# Revit family: QF_BPRO_RWRR 161_572938
name_source: partatom
category: Sonderausstattung
revit_build: Autodesk Revit 2018 (Build: 20190510_1515(x64)
units: mm (PartAtom-declared; Revit-internal decimal feet)

## family parameters
Arbeitsebenenbasiert = Nein
Beim Laden mit Abzugskörper schneiden = Nein
Bemaßung runder Anschluss = Durchmesser verwenden
Gemeinsam genutzt = Nein
Immer vertikal = Ja
Raumberechnungspunkt = Ja
Teiletyp = Normal

## types (1)
- RWRR 161
    Abstand Einlagen = 73 mm
    Anzahl Schienen = 18
    Artikel Nummer = 572938
    Beschreibung = Regalwagen aus rostfreiem Edelstahl
im leeren Zustand raumsparend ineinander zu schieben
Auflagenabstand: 18 Paar 73 mm
Kapazität: 18 GN 2/1 oder  36 GN 1/1
Tragfähigkeit: 200 kg
Wandabweiser aus Kunststoff (Polyamid) an allen vier Ecken
    Beschreibung durch Hersteller analog Leistungsverzeichniskurztext = Abmessungen

Länge:			 662 mm
Breite:			  734 mm
Höhe:			1645 mm

Lichtes Maß:
Abstand der Auflagenschienen:	    73 mm


Ausführung

Der Regalwagen besteht aus CNS 18/10, Werkstoff-Nr. 1.4301. Zwischen stabilem Vierkant-rohr mit 25 x 25 mm (gebogen ohne Einzug) befinden sich eingeschweißte U-Profil-Führungsschienen. Diese sind mit einer Kippsicherung sowie einer beidseitigen Durchschubsicherung für GN 2/1, 1/1 und 2/4 versehen.

Durch diagonal angeordnete Querverstrebungen
50 x 25 mm lassen sich die RWRR 161 im leeren Zustand raumsparend ineinander schieben.
Für zusätzliche Stabilität sorgen 2 einhängbare CNS-Bügel aus Rundmaterial, die auf der Vorder- und Rückseite auf halber Höhe angebracht sind und nach der Bestückung in die dafür vorgesehenen Ösen eingehängt werden.

Der Regalwagen ist fahrbar mittels rostfreien Kunststoffrollen gemäß DIN 18867, Teil 8
(4 Lenkrollen, davon 2 mit Feststeller, Rollendurchmesser 125 mm). Wandabweiser aus Kunststoff (Polyamid) an allen vier Ecken schützen vor Beschädigung.


Zubehör/ Optionen

•	Staubschutzhaube aus durchsichtigem PE (Best.Nr. 568 757)
•	Isolierhaube aus PE, beidseitig aluminiert (Best.Nr. 568 905)


 
Technische Daten

Werkstoff:		Chromnickelstahl 18/10,
		                        Polyamid (PA)
Materialstärke VK-Rohr:	1,5 mm
Materialstärke
Auflageschienen:		1,2 mm
Gewicht:		                        23,4 kg
Tragfähigkeit je Wagen:	200 kg
Anzahl Auflagenpaare:	18
Kapazität:	18 x GN 2/1 oder
		36 x GN 1/1


Besonderheit

•	U-Profil-Führungsschienen mit Kipp- und   beidseitiger Durchschubsicherung
•	im leeren Zustand raumsparend 
	ineinander zu schieben


Fabrikat

Hersteller:	B.PRO
Typ:                                       RWRR 161
Best.Nr.		572 938
    Beschreibung durch Hersteller analog Leistungsverzeichnislangtext = Abmessungen

Länge:			 662 mm
Breite:			  734 mm
Höhe:			1645 mm

Lichtes Maß:
Abstand der Auflagenschienen:	    73 mm


Ausführung

Der Regalwagen besteht aus CNS 18/10, Werkstoff-Nr. 1.4301. Zwischen stabilem Vierkant-rohr mit 25 x 25 mm (gebogen ohne Einzug) befinden sich eingeschweißte U-Profil-Führungsschienen. Diese sind mit einer Kippsicherung sowie einer beidseitigen Durchschubsicherung für GN 2/1, 1/1 und 2/4 versehen.

Durch diagonal angeordnete Querverstrebungen
50 x 25 mm lassen sich die RWRR 161 im leeren Zustand raumsparend ineinander schieben.
Für zusätzliche Stabilität sorgen 2 einhängbare CNS-Bügel aus Rundmaterial, die auf der Vorder- und Rückseite auf halber Höhe angebracht sind und nach der Bestückung in die dafür vorgesehenen Ösen eingehängt werden.

Der Regalwagen ist fahrbar mittels rostfreien Kunststoffrollen gemäß DIN 18867, Teil 8
(4 Lenkrollen, davon 2 mit Feststeller, Rollendurchmesser 125 mm). Wandabweiser aus Kunststoff (Polyamid) an allen vier Ecken schützen vor Beschädigung.


Zubehör/ Optionen

•	Staubschutzhaube aus durchsichtigem PE (Best.Nr. 568 757)
•	Isolierhaube aus PE, beidseitig aluminiert (Best.Nr. 568 905)


 
Technische Daten

Werkstoff:		Chromnickelstahl 18/10,
		                        Polyamid (PA)
Materialstärke VK-Rohr:	1,5 mm
Materialstärke
Auflageschienen:		1,2 mm
Gewicht:		                        23,4 kg
Tragfähigkeit je Wagen:	200 kg
Anzahl Auflagenpaare:	18
Kapazität:	18 x GN 2/1 oder
		36 x GN 1/1


Besonderheit

•	U-Profil-Führungsschienen mit Kipp- und   beidseitiger Durchschubsicherung
•	im leeren Zustand raumsparend 
	ineinander zu schieben


Fabrikat

Hersteller:	B.PRO
Typ:                                       RWRR 161
Best.Nr.		572 938
    Gerätegewicht Netto = 23.40 kg
    Großküchengerätezuordnung = Ja
    Hersteller = B.PRO GmbH
    Höhe = 1645 mm  [stored 5.39698 ft]
    Internetadresse Gerätehersteller = https://www.bpro-solutions.com
    Internetadresse für Ersatzteilliste = https://www.bpro-solutions.com
    Kosten = 848 $
    Länge Gerätebreite = 662 mm  [stored 2.17192 ft]
    Länge Korpus = 587 mm  [stored 1.92585 ft]
    Material = QF_Metal-Stainless-Steel_general
    Material_Stoßschutz = QF_Rubber-Black-Matt
    Modell = RWRR 161
    Sockelhöhe = 174 mm  [stored 0.570866 ft]
    Tiefe = 734 mm  [stored 2.40814 ft]
    Tiefe Korpus = 659 mm  [stored 2.16207 ft]
    Typenkommentare = Regalwagen, 1-teilig
    URL = https://www.bpro-solutions.com
    Versatz Einlage unten = 73 mm
    Zubehör = Nein

note: [stored X ft] marks values corroborated as IEEE doubles in the binary element streams (Revit-internal decimal feet)
